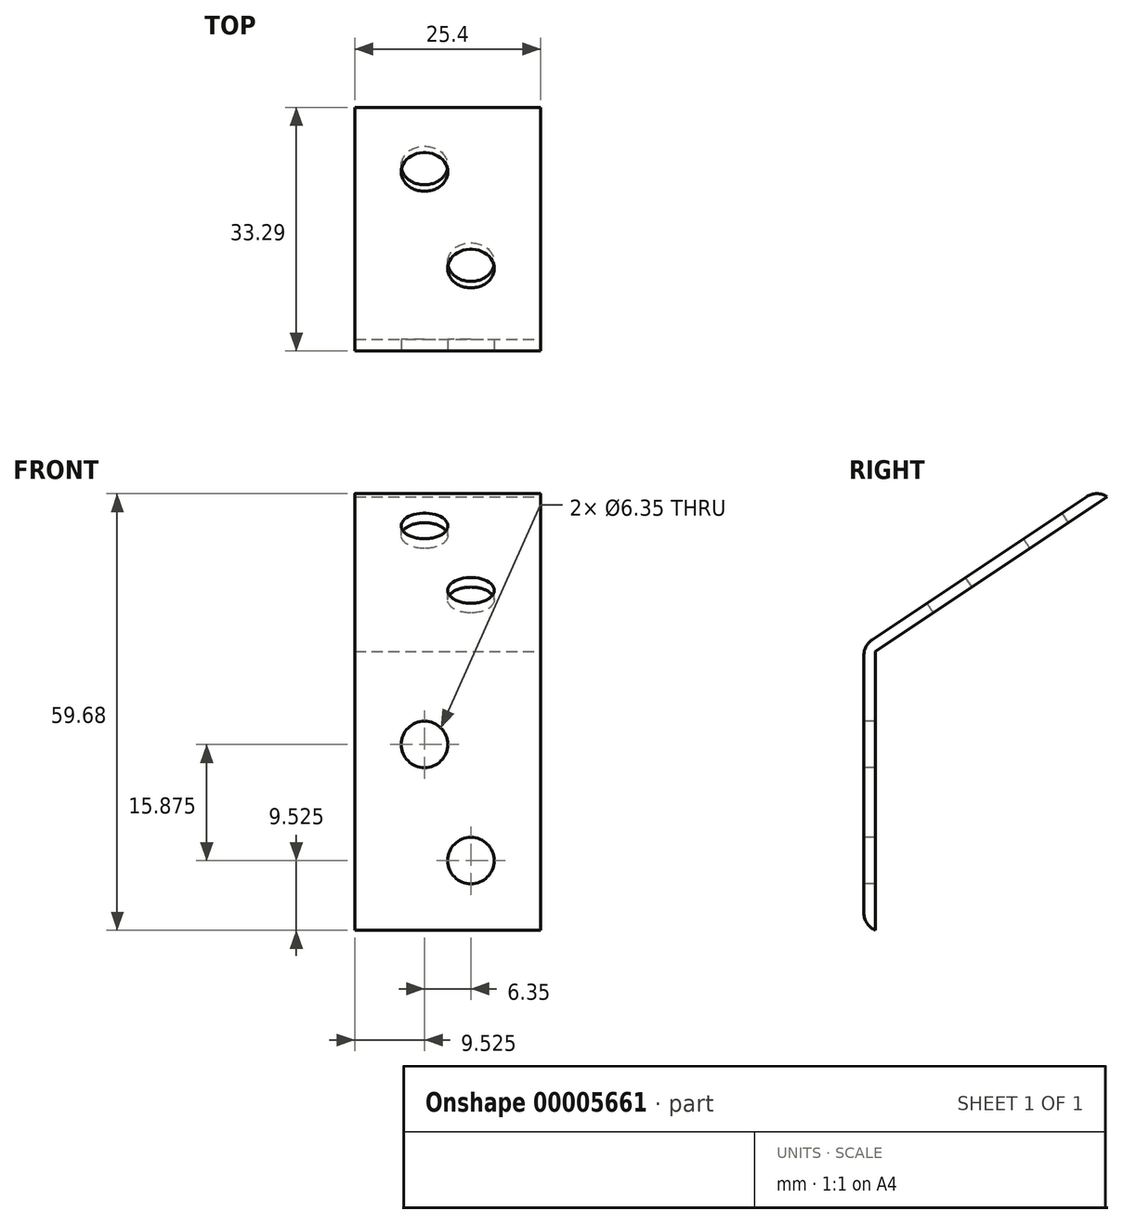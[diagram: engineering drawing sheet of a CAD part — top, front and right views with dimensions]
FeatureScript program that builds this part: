
annotation { "Feature Type Name" : "Feature", "Feature Type Description" : "" }
export const myFeature = defineFeature(function(context is Context, id is Id, definition is map)
    precondition{}
    {
        {
            var Q0;
            Q0=qCreatedBy(makeId("Right.planeOp"),FACE);
            var sketch = newSketch(context, id + "F0", { "sketchPlane" : qUnion([Q0])});
            skLineSegment(sketch, "E0.bottom", {"start": v(0, 0) * mm, "end": v(-1.59, 0) * mm});
            skLineSegment(sketch, "E0.left", {"start": v(0, 0) * mm, "end": v(0, 38.1) * mm});
            skLineSegment(sketch, "E0.right", {"start": v(-1.59, 0) * mm, "end": v(-1.59, 38.95) * mm});
            skLineSegment(sketch, "E1", {"start": v(0, 38.1) * mm, "end": v(31.7, 59.23) * mm});
            skLineSegment(sketch, "E2", {"start": v(31.7, 59.23) * mm, "end": v(30.82, 60.55) * mm});
            skLineSegment(sketch, "E3", {"start": v(30.82, 60.55) * mm, "end": v(-1.59, 38.95) * mm});
            skSolve(sketch);
        }
        {
            var Q0;
            Q0 = qSketchRegion(id + "F0", true);
            extrude(context, id + "F1", {"entities" : qUnion([Q0]), "oppositeDirection" : true, "depth" : 25.4 * mm});
        }
        {
            var Q0;
            Q0=makeQuery(id+"F1.opExtrude","SWEPT_FACE",FACE,{"disambiguationData":[OSD([sQuery(id+"F0.wireOp",EDGE,"E0.right")])]});
            var sketch = newSketch(context, id + "F2", { "sketchPlane" : qUnion([Q0])});
            skCircle(sketch, "E4", {"center": v(-15.88, 25.4) * mm, "radius": 3.18 * mm});
            skCircle(sketch, "E5", {"center": v(-9.53, 9.52) * mm, "radius": 3.18 * mm});
            skSolve(sketch);
        }
        {
            var Q0;
            Q0 = qSketchRegion(id + "F2", true);
            extrude(context, id + "F3", {"entities" : qUnion([Q0]), "operationType" : NewBodyOperationType.REMOVE, "oppositeDirection" : true, "depth" : 25.4 * mm});
        }
        {
            var Q0;
            Q0=makeQuery(id+"F1.opExtrude","SWEPT_FACE",FACE,{"disambiguationData":[OSD([sQuery(id+"F0.wireOp",EDGE,"E3")])]});
            var sketch = newSketch(context, id + "F4", { "sketchPlane" : qUnion([Q0])});
            skCircle(sketch, "E6", {"center": v(-9.53, 33.83) * mm, "radius": 3.18 * mm});
            skCircle(sketch, "E7", {"center": v(-15.88, 49.7) * mm, "radius": 3.18 * mm});
            skSolve(sketch);
        }
        {
            var Q0;
            Q0 = qSketchRegion(id + "F4", true);
            extrude(context, id + "F5", {"entities" : qUnion([Q0]), "operationType" : NewBodyOperationType.REMOVE, "oppositeDirection" : true, "depth" : 25.4 * mm});
        }
        {
            var Q0;
            Q0=makeQuery(id+"F1.opExtrude","SWEPT_EDGE",EDGE,{"disambiguationData":[OSD([sQuery(id+"F0.wireOp",EDGE,"E0.right"),sQuery(id+"F0.wireOp",EDGE,"E3")])]});
            var Q1;
            Q1=makeQuery(id+"F1.opExtrude","SWEPT_EDGE",EDGE,{"disambiguationData":[OSD([sQuery(id+"F0.wireOp",EDGE,"E2"),sQuery(id+"F0.wireOp",EDGE,"E3")])]});
            var Q2;
            Q2=makeQuery(id+"F1.opExtrude","SWEPT_EDGE",EDGE,{"disambiguationData":[OSD([sQuery(id+"F0.wireOp",EDGE,"E0.bottom"),sQuery(id+"F0.wireOp",EDGE,"E0.right")])]});
            fillet(context, id + "F6", {"entities" : qUnion([Q0, Q1, Q2]), "radius" : 2.54 * mm, "tangentPropagation" : true, "allowEdgeOverflow" : false});
        }
    });
